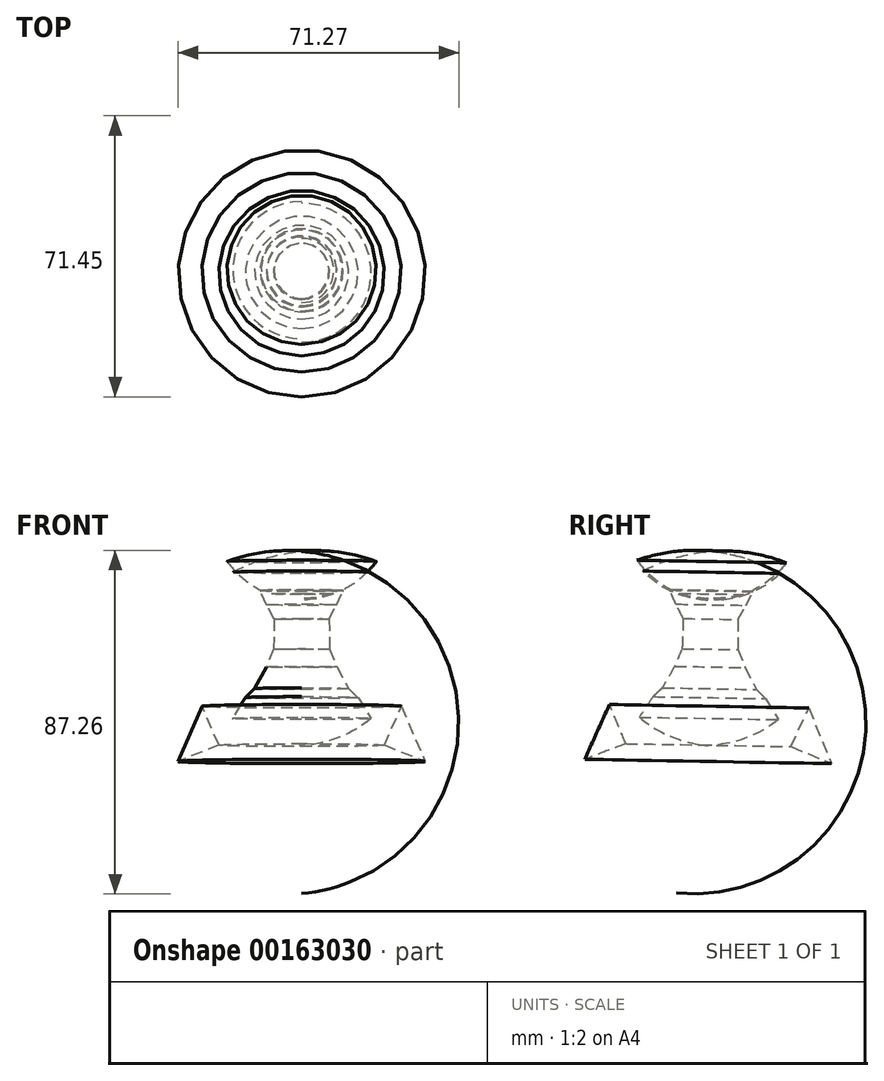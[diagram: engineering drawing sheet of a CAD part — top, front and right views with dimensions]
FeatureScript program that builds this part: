
annotation { "Feature Type Name" : "Feature", "Feature Type Description" : "" }
export const myFeature = defineFeature(function(context is Context, id is Id, definition is map)
    precondition{}
    {
        {
            var Q0;
            Q0=qCreatedBy(makeId("Right.planeOp"),FACE);
            var sketch = newSketch(context, id + "F0", { "sketchPlane" : qUnion([Q0])});
            skLineSegment(sketch, "E0", {"start": v(-17.98, -35.1) * mm, "end": v(-16.13, -31.73) * mm});
            skLineSegment(sketch, "E1", {"start": v(-16.13, -31.73) * mm, "end": v(-12.76, -28.24) * mm});
            skLineSegment(sketch, "E2", {"start": v(-12.76, -28.24) * mm, "end": v(-9.74, -23.02) * mm});
            skLineSegment(sketch, "E3", {"start": v(-9.74, -23.02) * mm, "end": v(-6.37, -13.84) * mm});
            skLineSegment(sketch, "E4", {"start": v(-6.37, -13.84) * mm, "end": v(-6.37, -10) * mm});
            skLineSegment(sketch, "E5", {"start": v(-6.37, -10) * mm, "end": v(-10.32, -3.61) * mm});
            skLineSegment(sketch, "E6", {"start": v(-10.32, -3.61) * mm, "end": v(-10.32, -1.52) * mm});
            skLineSegment(sketch, "E7", {"start": v(12.1, -1.4) * mm, "end": v(13.27, -2.45) * mm});
            skLineSegment(sketch, "E8", {"start": v(13.27, -2.45) * mm, "end": v(11.53, -5.94) * mm});
            skLineSegment(sketch, "E9", {"start": v(11.53, -5.94) * mm, "end": v(9.55, -9.54) * mm});
            skLineSegment(sketch, "E10", {"start": v(9.55, -9.54) * mm, "end": v(9.55, -12.1) * mm});
            skLineSegment(sketch, "E11", {"start": v(9.55, -12.1) * mm, "end": v(9.55, -17.2) * mm});
            skLineSegment(sketch, "E12", {"start": v(9.55, -17.2) * mm, "end": v(11.3, -21.74) * mm});
            skLineSegment(sketch, "E13", {"start": v(11.3, -21.74) * mm, "end": v(14.2, -27.31) * mm});
            skLineSegment(sketch, "E14", {"start": v(14.2, -27.31) * mm, "end": v(16.52, -29.64) * mm});
            skLineSegment(sketch, "E15", {"start": v(16.52, -29.64) * mm, "end": v(19.77, -34.98) * mm});
            skArc(sketch, "E16", {"start": v(-17.98, -35.1) * mm, "mid": v(0.91, -41.56) * mm, "end": v(19.77, -34.98) * mm});
            skArc(sketch, "E17", {"start": v(-16.13, -31.73) * mm, "mid": v(0.83, -36.26) * mm, "end": v(17.8, -31.73) * mm});
            skArc(sketch, "E18", {"start": v(-12.76, -28.24) * mm, "mid": v(0.72, -32.33) * mm, "end": v(14.2, -28.24) * mm});
            skArc(sketch, "E19", {"start": v(-10.32, -1.52) * mm, "mid": v(1.39, -4.2) * mm, "end": v(13.27, -2.45) * mm});
            skCircle(sketch, "E20", {"center": v(2.66, 19.4) * mm, "radius": 24.02 * mm});
            skLineSegment(sketch, "E21", {"start": v(3.5, 43.41) * mm, "end": v(1.6, -63.93) * mm});
            skLineSegment(sketch, "E22", {"start": v(-23.15, -31.14) * mm, "end": v(-17.73, -44.16) * mm});
            skLineSegment(sketch, "E23", {"start": v(-17.73, -44.16) * mm, "end": v(-23.15, -65.24) * mm});
            skLineSegment(sketch, "E24", {"start": v(-23.15, -65.24) * mm, "end": v(-29.44, -45.04) * mm});
            skLineSegment(sketch, "E25", {"start": v(-29.44, -45.04) * mm, "end": v(-23.15, -31.14) * mm});
            skLineSegment(sketch, "E26", {"start": v(-17.98, -33.41) * mm, "end": v(-23.15, -31.14) * mm});
            skPoint(sketch, "E26.startSnap0", {"position": v(-17.06, -33.41) * mm});
            skLineSegment(sketch, "E27", {"start": v(-17.73, -44.16) * mm, "end": v(-12.38, -38.57) * mm});
            skLineSegment(sketch, "E28", {"start": v(-12.38, -38.57) * mm, "end": v(-12.38, -65.54) * mm});
            skLineSegment(sketch, "E29", {"start": v(-12.38, -65.54) * mm, "end": v(-23.15, -65.54) * mm});
            skLineSegment(sketch, "E30", {"start": v(-29.44, -45.04) * mm, "end": v(-12.38, -38.57) * mm});
            skArc(sketch, "E31", {"start": v(-16.03, 34.5) * mm, "mid": v(3.2, 26.7) * mm, "end": v(23.4, 31.54) * mm});
            skArc(sketch, "E32", {"start": v(21.78, 4.86) * mm, "mid": v(3.33, 7.81) * mm, "end": v(-14.67, 2.78) * mm});
            skLineSegment(sketch, "E33", {"start": v(-13.59, 34.73) * mm, "end": v(-12.54, 36.2) * mm});
            skLineSegment(sketch, "E34", {"start": v(-12.54, 36.2) * mm, "end": v(-14.65, 33.4) * mm});
            skSolve(sketch);
        }
        {
            var Q0;
            {var subQ1=sQuery(id+"F0.wireOp",EDGE,"E7");var subQ3=sQuery(id+"F0.wireOp",EDGE,"E20");var subQ4=makeQuery(id+"F0.imprint","INTERSECT",VERTEX,{"derivedFrom":[subQ1,subQ3]});Q0=makeQuery(id+"F0.imprint","IMPRINT",FACE,{"disambiguationData":[TD([[makeQuery(id+"F0.imprint","IMPRINT",EDGE,{"disambiguationData":[TD([[subQ4,1.0]])],"derivedFrom":subQ3}),-1.0]])]});}
            var Q1;
            {var subQ0=sQuery(id+"F0.wireOp",EDGE,"E16");var subQ1=sQuery(id+"F0.wireOp",EDGE,"E15");var subQ2=makeQuery(id+"F0.imprint","INTERSECT",VERTEX,{"derivedFrom":[subQ1,subQ0]});Q1=makeQuery(id+"F0.imprint","IMPRINT",FACE,{"disambiguationData":[TD([[makeQuery(id+"F0.imprint","IMPRINT",EDGE,{"disambiguationData":[TD([[subQ2,1.0]])],"derivedFrom":subQ1}),-1.0]])]});}
            var Q2;
            {var subQ0=sQuery(id+"F0.wireOp",EDGE,"E20");var subQ1=sQuery(id+"F0.wireOp",EDGE,"E19");var subQ2=makeQuery(id+"F0.imprint","INTERSECT",VERTEX,{"disambiguationData":[OD(0.0)],"derivedFrom":[subQ1,subQ0]});Q2=makeQuery(id+"F0.imprint","IMPRINT",FACE,{"disambiguationData":[TD([[makeQuery(id+"F0.imprint","IMPRINT",EDGE,{"disambiguationData":[TD([[subQ2,-1.0]])],"derivedFrom":subQ1}),-1.0]])]});}
            var Q3;
            {var subQ0=sQuery(id+"F0.wireOp",EDGE,"E21");var subQ1=sQuery(id+"F0.wireOp",EDGE,"E19");var subQ2=makeQuery(id+"F0.imprint","INTERSECT",VERTEX,{"derivedFrom":[subQ1,subQ0]});Q3=makeQuery(id+"F0.imprint","IMPRINT",FACE,{"disambiguationData":[TD([[makeQuery(id+"F0.imprint","IMPRINT",EDGE,{"disambiguationData":[TD([[subQ2,-1.0]])],"derivedFrom":subQ1}),1.0]])]});}
            var Q4;
            {var subQ6=sQuery(id+"F0.wireOp",EDGE,"E8");Q4=makeQuery(id+"F0.imprint","IMPRINT",FACE,{"disambiguationData":[TD([[makeQuery(id+"F0.imprint","IMPRINT",EDGE,{"derivedFrom":subQ6}),-1.0]])]});}
            var Q5;
            Q5=makeQuery(id+"F0.imprint","IMPRINT",FACE,{"disambiguationData":[TD([[makeQuery(id+"F0.imprint","IMPRINT",EDGE,{"derivedFrom":sQuery(id+"F0.wireOp",EDGE,"E22")}),-1.0]])]});
            var Q6;
            {var subQ3=sQuery(id+"F0.wireOp",EDGE,"E31");var subQ6=makeQuery(id+"F0.imprint","IMPRINT",VERTEX,{"derivedFrom":subQ3});Q6=makeQuery(id+"F0.imprint","IMPRINT",FACE,{"disambiguationData":[TD([[makeQuery(id+"F0.imprint","IMPRINT",EDGE,{"disambiguationData":[TD([[subQ6,1.0]])],"derivedFrom":subQ3}),1.0]])]});}
            var Q7;
            {var subQ0=sQuery(id+"F0.wireOp",EDGE,"E31");var subQ1=makeQuery(id+"F0.imprint","IMPRINT",VERTEX,{"derivedFrom":subQ0});Q7=makeQuery(id+"F0.imprint","IMPRINT",FACE,{"disambiguationData":[TD([[makeQuery(id+"F0.imprint","IMPRINT",EDGE,{"disambiguationData":[TD([[subQ1,1.0]])],"derivedFrom":subQ0}),-1.0]])]});}
            var Q8;
            Q8=sQuery(id+"F0.wireOp",EDGE,"E21");
            revolve(context, id + "F1", {"entities" : qUnion([Q0, Q1, Q2, Q3, Q4, Q5, Q6, Q7]), "axis" : qUnion([Q8]), "revolveType" : RevolveType.FULL});
        }
    });
